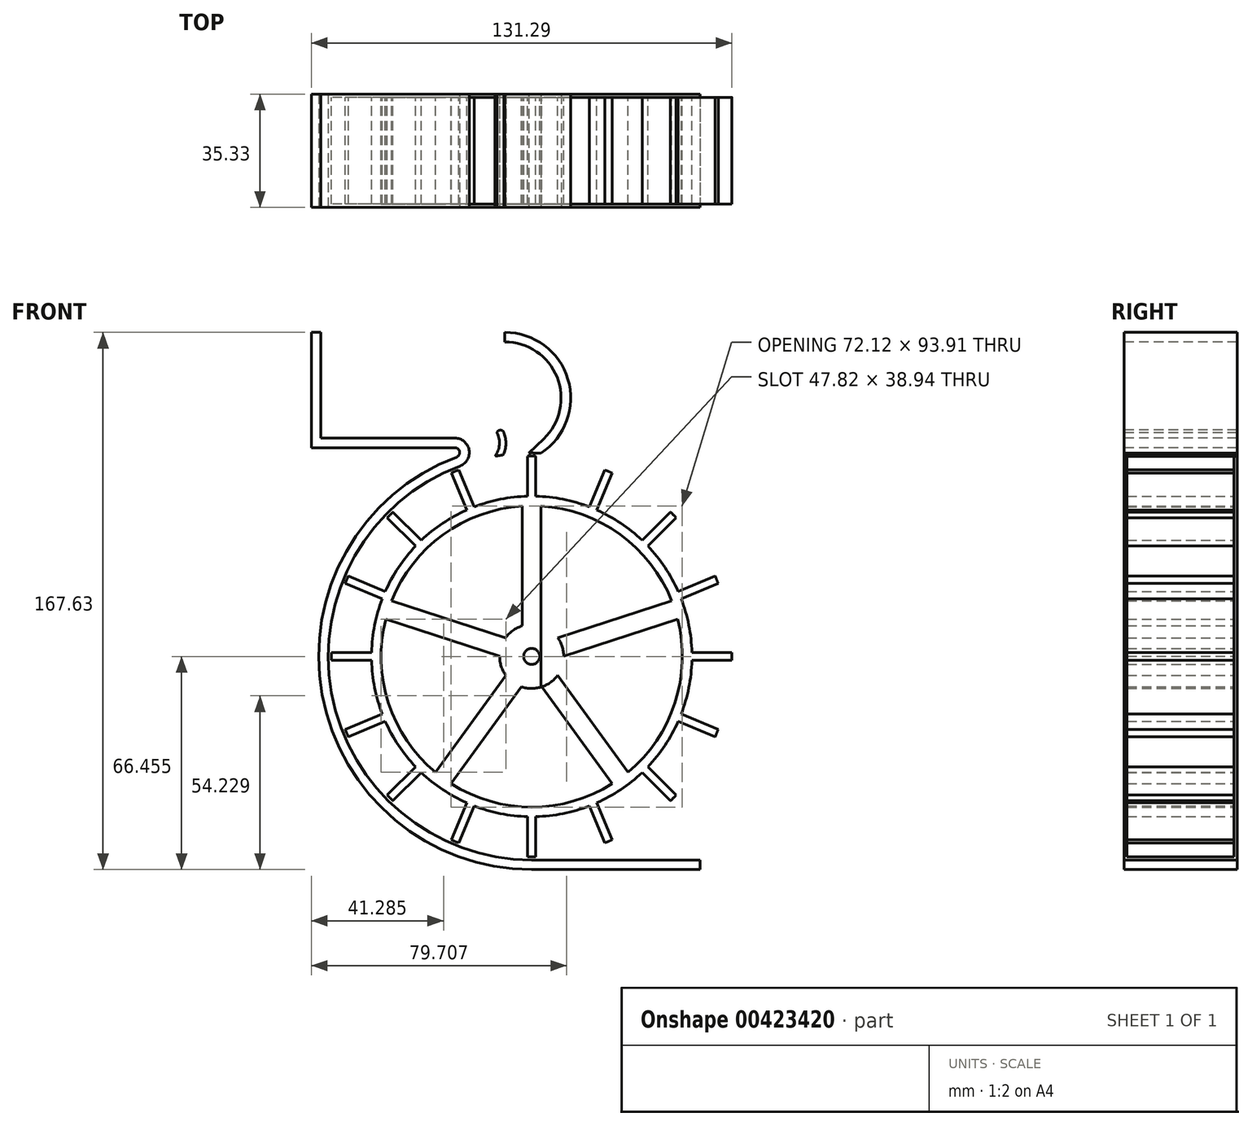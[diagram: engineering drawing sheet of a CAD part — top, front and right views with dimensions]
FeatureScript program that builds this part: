
annotation { "Feature Type Name" : "Feature", "Feature Type Description" : "" }
export const myFeature = defineFeature(function(context is Context, id is Id, definition is map)
    precondition{}
    {
        {
            var Q0;
            Q0=qCreatedBy(makeId("Front.planeOp"),FACE);
            var sketch = newSketch(context, id + "F0", { "sketchPlane" : qUnion([Q0])});
            skCircle(sketch, "E0", {"center": v(0, 0) * mm, "radius": 50 * mm});
            skCircle(sketch, "E1", {"center": v(0, 0) * mm, "radius": 62.5 * mm});
            skLineSegment(sketch, "E2", {"start": v(-50, 0) * mm, "end": v(-62.5, 0) * mm, "construction": true});
            skLineSegment(sketch, "E3.1.0", {"start": v(-43.3, -25) * mm, "end": v(-54.13, -31.25) * mm, "construction": true});
            skLineSegment(sketch, "E3.2.0", {"start": v(-25, -43.3) * mm, "end": v(-31.25, -54.13) * mm, "construction": true});
            skLineSegment(sketch, "E3.3.0", {"start": v(0, -50) * mm, "end": v(0, -62.5) * mm, "construction": true});
            skLineSegment(sketch, "E3.4.0", {"start": v(25, -43.3) * mm, "end": v(31.25, -54.13) * mm, "construction": true});
            skLineSegment(sketch, "E3.5.0", {"start": v(43.3, -25) * mm, "end": v(54.13, -31.25) * mm, "construction": true});
            skLineSegment(sketch, "E3.6.0", {"start": v(50, 0) * mm, "end": v(62.5, 0) * mm, "construction": true});
            skLineSegment(sketch, "E3.7.0", {"start": v(43.3, 25) * mm, "end": v(54.13, 31.25) * mm, "construction": true});
            skLineSegment(sketch, "E3.8.0", {"start": v(25, 43.3) * mm, "end": v(31.25, 54.13) * mm, "construction": true});
            skLineSegment(sketch, "E3.9.0", {"start": v(0, 50) * mm, "end": v(0, 62.5) * mm, "construction": true});
            skLineSegment(sketch, "E4.2.10.0", {"start": v(-25, 43.3) * mm, "end": v(-31.25, 54.13) * mm, "construction": true});
            skLineSegment(sketch, "E4.2.11.0", {"start": v(-43.3, 25) * mm, "end": v(-54.13, 31.25) * mm, "construction": true});
            skEllipse(sketch, "E5", {"center": v(-55.49, 11.06) * mm, "majorRadius": 10 * mm, "minorRadius": 5 * mm, "majorAxis": v(0.16, 0.99), "construction": true});
            skPoint(sketch, "E6.positionSnap0", {"position": v(-53.86, 20.93) * mm});
            skPoint(sketch, "E7.positionSnap0", {"position": v(-57.12, 1.2) * mm});
            skPoint(sketch, "E8", {"position": v(-60.42, 11.88) * mm});
            skPoint(sketch, "E9", {"position": v(-50.55, 10.25) * mm});
            skLineSegment(sketch, "E10", {"start": v(-49.98, 1.25) * mm, "end": v(-62.49, 1.25) * mm});
            skLineSegment(sketch, "E11", {"start": v(-49.98, -1.25) * mm, "end": v(-62.49, -1.25) * mm});
            skLineSegment(sketch, "E12.1.0", {"start": v(-46.66, -17.97) * mm, "end": v(-58.2, -22.76) * mm});
            skLineSegment(sketch, "E12.1.1", {"start": v(-45.7, -20.28) * mm, "end": v(-57.25, -25.07) * mm});
            skLineSegment(sketch, "E12.2.0", {"start": v(-36.23, -34.46) * mm, "end": v(-45.07, -43.3) * mm});
            skLineSegment(sketch, "E12.2.1", {"start": v(-34.46, -36.23) * mm, "end": v(-43.3, -45.07) * mm});
            skLineSegment(sketch, "E12.3.0", {"start": v(-20.28, -45.7) * mm, "end": v(-25.07, -57.25) * mm});
            skLineSegment(sketch, "E12.3.1", {"start": v(-17.97, -46.66) * mm, "end": v(-22.76, -58.2) * mm});
            skLineSegment(sketch, "E12.4.0", {"start": v(-1.25, -49.98) * mm, "end": v(-1.25, -62.49) * mm});
            skLineSegment(sketch, "E12.4.1", {"start": v(1.25, -49.98) * mm, "end": v(1.25, -62.49) * mm});
            skLineSegment(sketch, "E12.5.0", {"start": v(17.97, -46.66) * mm, "end": v(22.76, -58.2) * mm});
            skLineSegment(sketch, "E12.5.1", {"start": v(20.28, -45.7) * mm, "end": v(25.07, -57.25) * mm});
            skLineSegment(sketch, "E12.6.0", {"start": v(34.46, -36.23) * mm, "end": v(43.3, -45.07) * mm});
            skLineSegment(sketch, "E12.6.1", {"start": v(36.23, -34.46) * mm, "end": v(45.07, -43.3) * mm});
            skLineSegment(sketch, "E12.7.0", {"start": v(45.7, -20.28) * mm, "end": v(57.25, -25.07) * mm});
            skLineSegment(sketch, "E12.7.1", {"start": v(46.66, -17.97) * mm, "end": v(58.2, -22.76) * mm});
            skLineSegment(sketch, "E12.8.0", {"start": v(49.98, -1.25) * mm, "end": v(62.49, -1.25) * mm});
            skLineSegment(sketch, "E12.8.1", {"start": v(49.98, 1.25) * mm, "end": v(62.49, 1.25) * mm});
            skLineSegment(sketch, "E12.9.0", {"start": v(46.66, 17.97) * mm, "end": v(58.2, 22.76) * mm});
            skLineSegment(sketch, "E12.9.1", {"start": v(45.7, 20.28) * mm, "end": v(57.25, 25.07) * mm});
            skLineSegment(sketch, "E12.10.0", {"start": v(36.23, 34.46) * mm, "end": v(45.07, 43.3) * mm});
            skLineSegment(sketch, "E12.10.1", {"start": v(34.46, 36.23) * mm, "end": v(43.3, 45.07) * mm});
            skLineSegment(sketch, "E12.11.0", {"start": v(20.28, 45.7) * mm, "end": v(25.07, 57.25) * mm});
            skLineSegment(sketch, "E12.11.1", {"start": v(17.97, 46.66) * mm, "end": v(22.76, 58.2) * mm});
            skCircle(sketch, "E13", {"center": v(0, 0) * mm, "radius": 47 * mm});
            skCircle(sketch, "E14", {"center": v(0, 0) * mm, "radius": 10 * mm});
            skLineSegment(sketch, "E15", {"start": v(-3, 9.54) * mm, "end": v(-3, 46.9) * mm});
            skLineSegment(sketch, "E16", {"start": v(3, 46.9) * mm, "end": v(3, 9.54) * mm});
            skCircle(sketch, "E17", {"center": v(0, 0) * mm, "radius": 2.5 * mm});
            skLineSegment(sketch, "E18.1.0", {"start": v(-43.68, 17.35) * mm, "end": v(-8.15, 5.8) * mm});
            skLineSegment(sketch, "E18.1.1", {"start": v(-10, 0.1) * mm, "end": v(-45.54, 11.64) * mm});
            skLineSegment(sketch, "E18.2.0", {"start": v(-30, -36.18) * mm, "end": v(-8.03, -5.95) * mm});
            skLineSegment(sketch, "E18.2.1", {"start": v(-3.18, -9.48) * mm, "end": v(-25.14, -39.7) * mm});
            skLineSegment(sketch, "E18.3.0", {"start": v(25.14, -39.7) * mm, "end": v(3.18, -9.48) * mm});
            skLineSegment(sketch, "E18.3.1", {"start": v(8.03, -5.95) * mm, "end": v(30, -36.18) * mm});
            skLineSegment(sketch, "E18.4.0", {"start": v(45.54, 11.64) * mm, "end": v(10, 0.1) * mm});
            skLineSegment(sketch, "E18.4.1", {"start": v(8.15, 5.8) * mm, "end": v(43.68, 17.35) * mm});
            skArc(sketch, "E19", {"start": v(0, 65.2) * mm, "mid": v(8.63, 84.91) * mm, "end": v(-8.36, 98.13) * mm});
            skLineSegment(sketch, "E20", {"start": v(-8.36, 98.13) * mm, "end": v(-31.16, 98.13) * mm});
            skArc(sketch, "E21", {"start": v(2.9, 63.43) * mm, "mid": v(-1.83, 63.47) * mm, "end": v(-6.55, 63.16) * mm});
            skArc(sketch, "E22", {"start": v(2.9, 63.43) * mm, "mid": v(11.3, 86.48) * mm, "end": v(-8.36, 101.13) * mm});
            skLineSegment(sketch, "E23", {"start": v(-8.36, 101.13) * mm, "end": v(-31.16, 101.13) * mm});
            skLineSegment(sketch, "E24", {"start": v(-31.16, 101.13) * mm, "end": v(-31.16, 98.13) * mm, "construction": true});
            skArc(sketch, "E25", {"start": v(-6.55, 63.16) * mm, "mid": v(-11.47, 62.45) * mm, "end": v(-16.32, 61.37) * mm, "construction": true});
            skArc(sketch, "E26", {"start": v(-22.4, 59.42) * mm, "mid": v(-19.55, 64.44) * mm, "end": v(-23.98, 68.13) * mm});
            skLineSegment(sketch, "E27", {"start": v(-23.98, 68.13) * mm, "end": v(-65.8, 68.13) * mm});
            skLineSegment(sketch, "E28", {"start": v(-68.8, 68.13) * mm, "end": v(-68.8, 65.13) * mm});
            skLineSegment(sketch, "E29", {"start": v(-68.8, 65.13) * mm, "end": v(-23.98, 65.13) * mm});
            skArc(sketch, "E30", {"start": v(-23.45, 62.23) * mm, "mid": v(-22.5, 63.9) * mm, "end": v(-23.98, 65.13) * mm});
            skArc(sketch, "E31", {"start": v(-23.45, 62.23) * mm, "mid": v(-65.42, -11.92) * mm, "end": v(0, -66.5) * mm});
            skArc(sketch, "E32", {"start": v(-22.4, 59.42) * mm, "mid": v(-62.47, -11.38) * mm, "end": v(0, -63.5) * mm});
            skLineSegment(sketch, "E33", {"start": v(0, -63.5) * mm, "end": v(0, -66.5) * mm, "construction": true});
            skLineSegment(sketch, "E34", {"start": v(0, -63.5) * mm, "end": v(52.47, -63.5) * mm});
            skLineSegment(sketch, "E35", {"start": v(52.47, -63.5) * mm, "end": v(52.47, -66.5) * mm});
            skLineSegment(sketch, "E36", {"start": v(52.47, -66.5) * mm, "end": v(0, -66.5) * mm});
            skLineSegment(sketch, "E37", {"start": v(2.9, 63.43) * mm, "end": v(2.9, -45.35) * mm});
            skLineSegment(sketch, "E38", {"start": v(2.9, -45.35) * mm, "end": v(52.47, -45.35) * mm});
            skLineSegment(sketch, "E39", {"start": v(52.47, -45.35) * mm, "end": v(52.47, -63.5) * mm});
            skLineSegment(sketch, "E40", {"start": v(0, 65.2) * mm, "end": v(-0.88, 63.5) * mm, "construction": true});
            skLineSegment(sketch, "E41", {"start": v(-0.88, 63.5) * mm, "end": v(3.76, 67.94) * mm});
            skLineSegment(sketch, "E42", {"start": v(-8.36, 101.13) * mm, "end": v(-8.36, 98.13) * mm});
            skArc(sketch, "E43", {"start": v(-11.47, 62.45) * mm, "mid": v(-10.1, 66.01) * mm, "end": v(-10.86, 69.76) * mm});
            skArc(sketch, "E44", {"start": v(-8.89, 62.88) * mm, "mid": v(-8.07, 66.3) * mm, "end": v(-8.66, 69.76) * mm});
            skArc(sketch, "E45", {"start": v(-8.66, 69.76) * mm, "mid": v(-9.76, 70.63) * mm, "end": v(-10.86, 69.76) * mm});
            skArc(sketch, "E46", {"start": v(-11.47, 62.45) * mm, "mid": v(-10.18, 62.68) * mm, "end": v(-8.89, 62.88) * mm});
            skLineSegment(sketch, "E47", {"start": v(-68.8, 68.13) * mm, "end": v(-68.8, 101.13) * mm});
            skLineSegment(sketch, "E48", {"start": v(-68.8, 101.13) * mm, "end": v(-65.8, 101.13) * mm});
            skLineSegment(sketch, "E49", {"start": v(-65.8, 101.13) * mm, "end": v(-65.8, 68.13) * mm});
            skLineSegment(sketch, "E50.3.12.0", {"start": v(-1.25, 49.98) * mm, "end": v(-1.25, 62.49) * mm});
            skLineSegment(sketch, "E50.5.12.0", {"start": v(1.25, 49.98) * mm, "end": v(1.25, 62.49) * mm});
            skLineSegment(sketch, "E50.3.13.0", {"start": v(-20.28, 45.7) * mm, "end": v(-25.07, 57.25) * mm});
            skLineSegment(sketch, "E50.5.13.0", {"start": v(-17.97, 46.66) * mm, "end": v(-22.76, 58.2) * mm});
            skLineSegment(sketch, "E50.3.14.0", {"start": v(-36.23, 34.46) * mm, "end": v(-45.07, 43.3) * mm});
            skLineSegment(sketch, "E50.5.14.0", {"start": v(-34.46, 36.23) * mm, "end": v(-43.3, 45.07) * mm});
            skLineSegment(sketch, "E50.3.15.0", {"start": v(-46.66, 17.97) * mm, "end": v(-58.2, 22.76) * mm});
            skLineSegment(sketch, "E50.5.15.0", {"start": v(-45.7, 20.28) * mm, "end": v(-57.25, 25.07) * mm});
            skSolve(sketch);
        }
        {
            var Q0;
            Q0=makeQuery(id+"F0.imprint","IMPRINT",FACE,{"disambiguationData":[TD([[makeQuery(id+"F0.imprint","IMPRINT",EDGE,{"derivedFrom":sQuery(id+"F0.wireOp",EDGE,"E13")}),-1.0]])]});
            var Q1;
            {var subQ0=sQuery(id+"F0.wireOp",EDGE,"E12.11.0");Q1=makeQuery(id+"F0.imprint","IMPRINT",FACE,{"disambiguationData":[TD([[makeQuery(id+"F0.imprint","IMPRINT",EDGE,{"derivedFrom":subQ0}),1.0]])]});}
            var Q2;
            {var subQ0=sQuery(id+"F0.wireOp",EDGE,"E10");Q2=makeQuery(id+"F0.imprint","IMPRINT",FACE,{"disambiguationData":[TD([[makeQuery(id+"F0.imprint","IMPRINT",EDGE,{"derivedFrom":subQ0}),1.0]])]});}
            var Q3;
            {var subQ0=sQuery(id+"F0.wireOp",EDGE,"E12.1.0");Q3=makeQuery(id+"F0.imprint","IMPRINT",FACE,{"disambiguationData":[TD([[makeQuery(id+"F0.imprint","IMPRINT",EDGE,{"derivedFrom":subQ0}),1.0]])]});}
            var Q4;
            {var subQ0=sQuery(id+"F0.wireOp",EDGE,"E12.2.0");Q4=makeQuery(id+"F0.imprint","IMPRINT",FACE,{"disambiguationData":[TD([[makeQuery(id+"F0.imprint","IMPRINT",EDGE,{"derivedFrom":subQ0}),1.0]])]});}
            var Q5;
            {var subQ0=sQuery(id+"F0.wireOp",EDGE,"E12.3.0");Q5=makeQuery(id+"F0.imprint","IMPRINT",FACE,{"disambiguationData":[TD([[makeQuery(id+"F0.imprint","IMPRINT",EDGE,{"derivedFrom":subQ0}),1.0]])]});}
            var Q6;
            {var subQ0=sQuery(id+"F0.wireOp",EDGE,"E12.4.0");Q6=makeQuery(id+"F0.imprint","IMPRINT",FACE,{"disambiguationData":[TD([[makeQuery(id+"F0.imprint","IMPRINT",EDGE,{"derivedFrom":subQ0}),1.0]])]});}
            var Q7;
            {var subQ0=sQuery(id+"F0.wireOp",EDGE,"E12.5.0");Q7=makeQuery(id+"F0.imprint","IMPRINT",FACE,{"disambiguationData":[TD([[makeQuery(id+"F0.imprint","IMPRINT",EDGE,{"derivedFrom":subQ0}),1.0]])]});}
            var Q8;
            {var subQ0=sQuery(id+"F0.wireOp",EDGE,"E12.6.0");Q8=makeQuery(id+"F0.imprint","IMPRINT",FACE,{"disambiguationData":[TD([[makeQuery(id+"F0.imprint","IMPRINT",EDGE,{"derivedFrom":subQ0}),1.0]])]});}
            var Q9;
            {var subQ0=sQuery(id+"F0.wireOp",EDGE,"E12.7.0");Q9=makeQuery(id+"F0.imprint","IMPRINT",FACE,{"disambiguationData":[TD([[makeQuery(id+"F0.imprint","IMPRINT",EDGE,{"derivedFrom":subQ0}),1.0]])]});}
            var Q10;
            {var subQ0=sQuery(id+"F0.wireOp",EDGE,"E12.8.0");Q10=makeQuery(id+"F0.imprint","IMPRINT",FACE,{"disambiguationData":[TD([[makeQuery(id+"F0.imprint","IMPRINT",EDGE,{"derivedFrom":subQ0}),1.0]])]});}
            var Q11;
            {var subQ0=sQuery(id+"F0.wireOp",EDGE,"E12.9.0");Q11=makeQuery(id+"F0.imprint","IMPRINT",FACE,{"disambiguationData":[TD([[makeQuery(id+"F0.imprint","IMPRINT",EDGE,{"derivedFrom":subQ0}),1.0]])]});}
            var Q12;
            {var subQ0=sQuery(id+"F0.wireOp",EDGE,"E12.10.0");Q12=makeQuery(id+"F0.imprint","IMPRINT",FACE,{"disambiguationData":[TD([[makeQuery(id+"F0.imprint","IMPRINT",EDGE,{"derivedFrom":subQ0}),1.0]])]});}
            var Q13;
            {var subQ0=sQuery(id+"F0.wireOp",EDGE,"E18.1.0");Q13=makeQuery(id+"F0.imprint","IMPRINT",FACE,{"disambiguationData":[TD([[makeQuery(id+"F0.imprint","IMPRINT",EDGE,{"derivedFrom":subQ0}),-1.0]])]});}
            var Q14;
            {var subQ0=sQuery(id+"F0.wireOp",EDGE,"E18.2.0");Q14=makeQuery(id+"F0.imprint","IMPRINT",FACE,{"disambiguationData":[TD([[makeQuery(id+"F0.imprint","IMPRINT",EDGE,{"derivedFrom":subQ0}),-1.0]])]});}
            var Q15;
            {var subQ0=sQuery(id+"F0.wireOp",EDGE,"E18.3.0");Q15=makeQuery(id+"F0.imprint","IMPRINT",FACE,{"disambiguationData":[TD([[makeQuery(id+"F0.imprint","IMPRINT",EDGE,{"derivedFrom":subQ0}),-1.0]])]});}
            var Q16;
            {var subQ0=sQuery(id+"F0.wireOp",EDGE,"E18.4.0");Q16=makeQuery(id+"F0.imprint","IMPRINT",FACE,{"disambiguationData":[TD([[makeQuery(id+"F0.imprint","IMPRINT",EDGE,{"derivedFrom":subQ0}),-1.0]])]});}
            var Q17;
            {var subQ0=sQuery(id+"F0.wireOp",EDGE,"E15");Q17=makeQuery(id+"F0.imprint","IMPRINT",FACE,{"disambiguationData":[TD([[makeQuery(id+"F0.imprint","IMPRINT",EDGE,{"derivedFrom":subQ0}),-1.0]])]});}
            var Q18;
            Q18=makeQuery(id+"F0.imprint","IMPRINT",FACE,{"disambiguationData":[TD([[makeQuery(id+"F0.imprint","IMPRINT",EDGE,{"derivedFrom":sQuery(id+"F0.wireOp",EDGE,"E17")}),-1.0]])]});
            var Q19;
            {var subQ0=sQuery(id+"F0.wireOp",EDGE,"E14");var subQ3=makeQuery(id+"F0.imprint","IMPRINT",VERTEX,{"derivedFrom":subQ0});Q19=makeQuery(id+"F0.imprint","IMPRINT",FACE,{"disambiguationData":[TD([[makeQuery(id+"F0.imprint","IMPRINT",EDGE,{"disambiguationData":[TD([[subQ3,1.0]])],"derivedFrom":subQ0}),1.0]])]});}
            var Q20;
            {var subQ0=sQuery(id+"F0.wireOp",EDGE,"E18.3.1");Q20=makeQuery(id+"F0.imprint","IMPRINT",FACE,{"disambiguationData":[TD([[makeQuery(id+"F0.imprint","IMPRINT",EDGE,{"derivedFrom":subQ0}),-1.0]])]});}
            var Q21;
            {var subQ0=sQuery(id+"F0.wireOp",EDGE,"E0");var subQ9=makeQuery(id+"F0.imprint","IMPRINT",VERTEX,{"derivedFrom":subQ0});Q21=makeQuery(id+"F0.imprint","IMPRINT",FACE,{"disambiguationData":[TD([[makeQuery(id+"F0.imprint","IMPRINT",EDGE,{"disambiguationData":[TD([[subQ9,1.0]])],"derivedFrom":subQ0}),1.0]])]});}
            var Q22;
            {var subQ0=sQuery(id+"F0.wireOp",EDGE,"E0");var subQ2=makeQuery(id+"F0.imprint","INTERSECT",VERTEX,{"derivedFrom":[subQ0,sQuery(id+"F0.wireOp",EDGE,"E12.3.1")]});Q22=makeQuery(id+"F0.imprint","IMPRINT",FACE,{"disambiguationData":[TD([[makeQuery(id+"F0.imprint","IMPRINT",EDGE,{"disambiguationData":[TD([[subQ2,-1.0]])],"derivedFrom":subQ0}),1.0]])]});}
            var Q23;
            {var subQ0=sQuery(id+"F0.wireOp",EDGE,"E50.3.15.0");Q23=makeQuery(id+"F0.imprint","IMPRINT",FACE,{"disambiguationData":[TD([[makeQuery(id+"F0.imprint","IMPRINT",EDGE,{"derivedFrom":subQ0}),-1.0]])]});}
            var Q24;
            {var subQ0=sQuery(id+"F0.wireOp",EDGE,"E50.3.14.0");Q24=makeQuery(id+"F0.imprint","IMPRINT",FACE,{"disambiguationData":[TD([[makeQuery(id+"F0.imprint","IMPRINT",EDGE,{"derivedFrom":subQ0}),-1.0]])]});}
            var Q25;
            {var subQ0=sQuery(id+"F0.wireOp",EDGE,"E50.3.13.0");Q25=makeQuery(id+"F0.imprint","IMPRINT",FACE,{"disambiguationData":[TD([[makeQuery(id+"F0.imprint","IMPRINT",EDGE,{"derivedFrom":subQ0}),-1.0]])]});}
            var Q26;
            {var subQ0=sQuery(id+"F0.wireOp",EDGE,"E50.3.12.0");Q26=makeQuery(id+"F0.imprint","IMPRINT",FACE,{"disambiguationData":[TD([[makeQuery(id+"F0.imprint","IMPRINT",EDGE,{"derivedFrom":subQ0}),-1.0]])]});}
            extrude(context, id + "F1", {"entities" : qUnion([Q0, Q1, Q2, Q3, Q4, Q5, Q6, Q7, Q8, Q9, Q10, Q11, Q12, Q13, Q14, Q15, Q16, Q17, Q18, Q19, Q20, Q21, Q22, Q23, Q24, Q25, Q26]), "depth" : (1000 / 30) * mm, "offsetDistance" : 25 * mm});
        }
        {
            var Q0;
            {var subQ4=sQuery(id+"F0.wireOp",EDGE,"E20");Q0=makeQuery(id+"F0.imprint","IMPRINT",FACE,{"disambiguationData":[TD([[makeQuery(id+"F0.imprint","IMPRINT",EDGE,{"derivedFrom":subQ4}),-1.0]])]});}
            var Q1;
            Q1=makeQuery(id+"F0.imprint","IMPRINT",FACE,{"disambiguationData":[TD([[makeQuery(id+"F0.imprint","IMPRINT",EDGE,{"derivedFrom":sQuery(id+"F0.wireOp",EDGE,"E26")}),1.0]])]});
            var Q2;
            {var subQ1=sQuery(id+"F0.wireOp",EDGE,"E22");Q2=makeQuery(id+"F0.imprint","IMPRINT",FACE,{"disambiguationData":[TD([[makeQuery(id+"F0.imprint","IMPRINT",EDGE,{"derivedFrom":subQ1}),1.0]])]});}
            var Q3;
            Q3=makeQuery(id+"F0.imprint","IMPRINT",FACE,{"disambiguationData":[TD([[makeQuery(id+"F0.imprint","IMPRINT",EDGE,{"derivedFrom":sQuery(id+"F0.wireOp",EDGE,"E43")}),-1.0]])]});
            extrude(context, id + "F2", {"entities" : qUnion([Q0, Q1, Q2, Q3]), "oppositeDirection" : true, "depth" : 1 * mm, "offsetDistance" : 25 * mm, "hasSecondDirection" : true, "secondDirectionOppositeDirection" : false, "secondDirectionDepth" : (1000 / 30 + 1) * mm});
        }
    });
